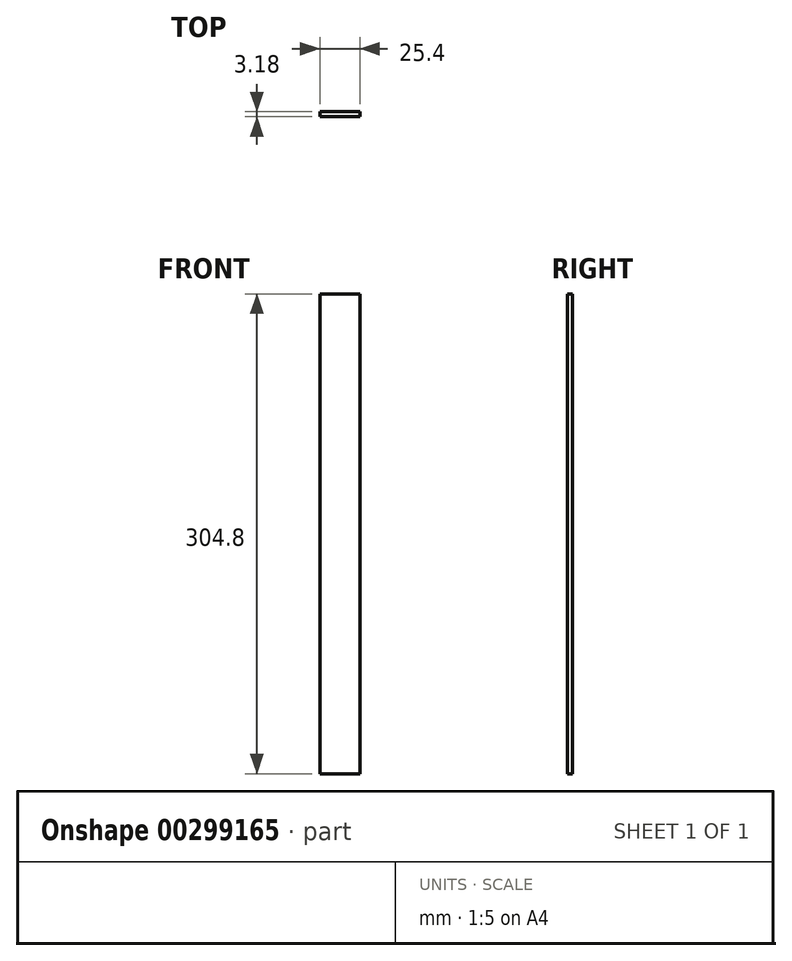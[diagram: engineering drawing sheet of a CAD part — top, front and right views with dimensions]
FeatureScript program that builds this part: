
annotation { "Feature Type Name" : "Feature", "Feature Type Description" : "" }
export const myFeature = defineFeature(function(context is Context, id is Id, definition is map)
    precondition{}
    {
        {
            var Q0;
            Q0=qCreatedBy(makeId("Front.planeOp"),FACE);
            var sketch = newSketch(context, id + "F0", { "sketchPlane" : qUnion([Q0])});
            skLineSegment(sketch, "E0.bottom", {"start": v(-12.7, 152.4) * mm, "end": v(12.7, 152.4) * mm});
            skLineSegment(sketch, "E0.top", {"start": v(-12.7, -152.4) * mm, "end": v(12.7, -152.4) * mm});
            skLineSegment(sketch, "E0.left", {"start": v(-12.7, 152.4) * mm, "end": v(-12.7, -152.4) * mm});
            skLineSegment(sketch, "E0.right", {"start": v(12.7, 152.4) * mm, "end": v(12.7, -152.4) * mm});
            skPoint(sketch, "E0.middle", {"position": v(0, 0) * mm});
            skSolve(sketch);
        }
        {
            var Q0;
            Q0=makeQuery(id+"F0.imprint","IMPRINT",FACE,{"disambiguationData":[TD([[makeQuery(id+"F0.imprint","IMPRINT",EDGE,{"derivedFrom":sQuery(id+"F0.wireOp",EDGE,"E0.bottom")}),-1.0]])]});
            extrude(context, id + "F1", {"entities" : qUnion([Q0]), "endBound" : BoundingType.SYMMETRIC, "depth" : 3.17 * mm});
        }
    });
